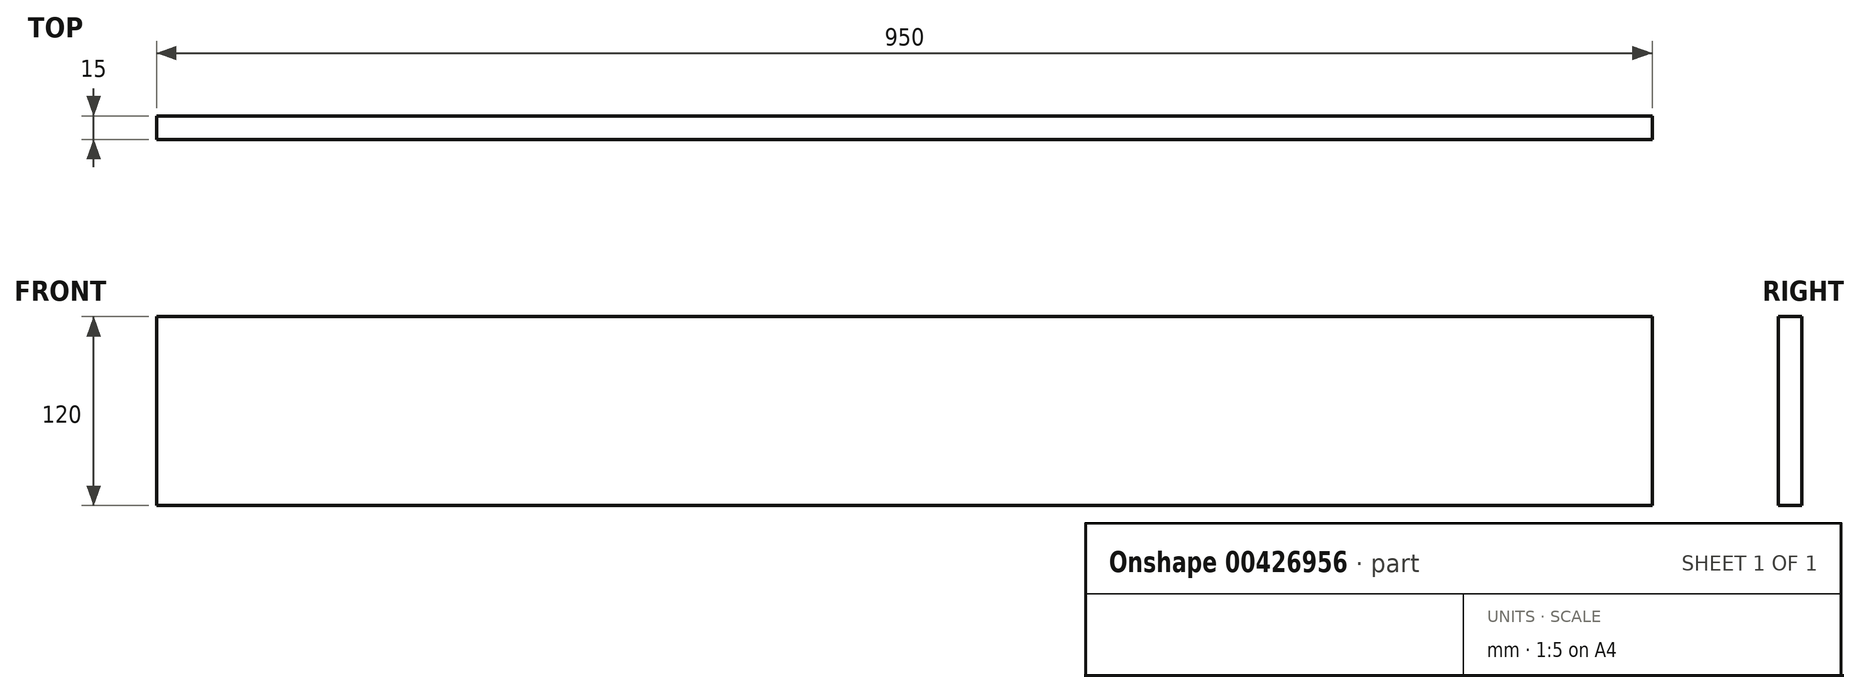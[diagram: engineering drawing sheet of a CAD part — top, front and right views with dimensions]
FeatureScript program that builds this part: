
annotation { "Feature Type Name" : "Feature", "Feature Type Description" : "" }
export const myFeature = defineFeature(function(context is Context, id is Id, definition is map)
    precondition{}
    {
        {
            var Q0;
            Q0=qCreatedBy(makeId("Front.planeOp"),FACE);
            var sketch = newSketch(context, id + "F0", { "sketchPlane" : qUnion([Q0])});
            skLineSegment(sketch, "E0.bottom", {"start": v(-515.39, -61.8) * mm, "end": v(434.61, -61.8) * mm});
            skLineSegment(sketch, "E0.top", {"start": v(-515.39, -181.8) * mm, "end": v(434.61, -181.8) * mm});
            skLineSegment(sketch, "E0.left", {"start": v(-515.39, -61.8) * mm, "end": v(-515.39, -181.8) * mm});
            skLineSegment(sketch, "E0.right", {"start": v(434.61, -61.8) * mm, "end": v(434.61, -181.8) * mm});
            skSolve(sketch);
        }
        {
            var Q0;
            Q0=makeQuery(id+"F0.imprint","IMPRINT",FACE,{"disambiguationData":[TD([[makeQuery(id+"F0.imprint","IMPRINT",EDGE,{"derivedFrom":sQuery(id+"F0.wireOp",EDGE,"E0.bottom")}),-1.0]])]});
            extrude(context, id + "F1", {"entities" : qUnion([Q0]), "depth" : 15 * mm});
        }
    });
